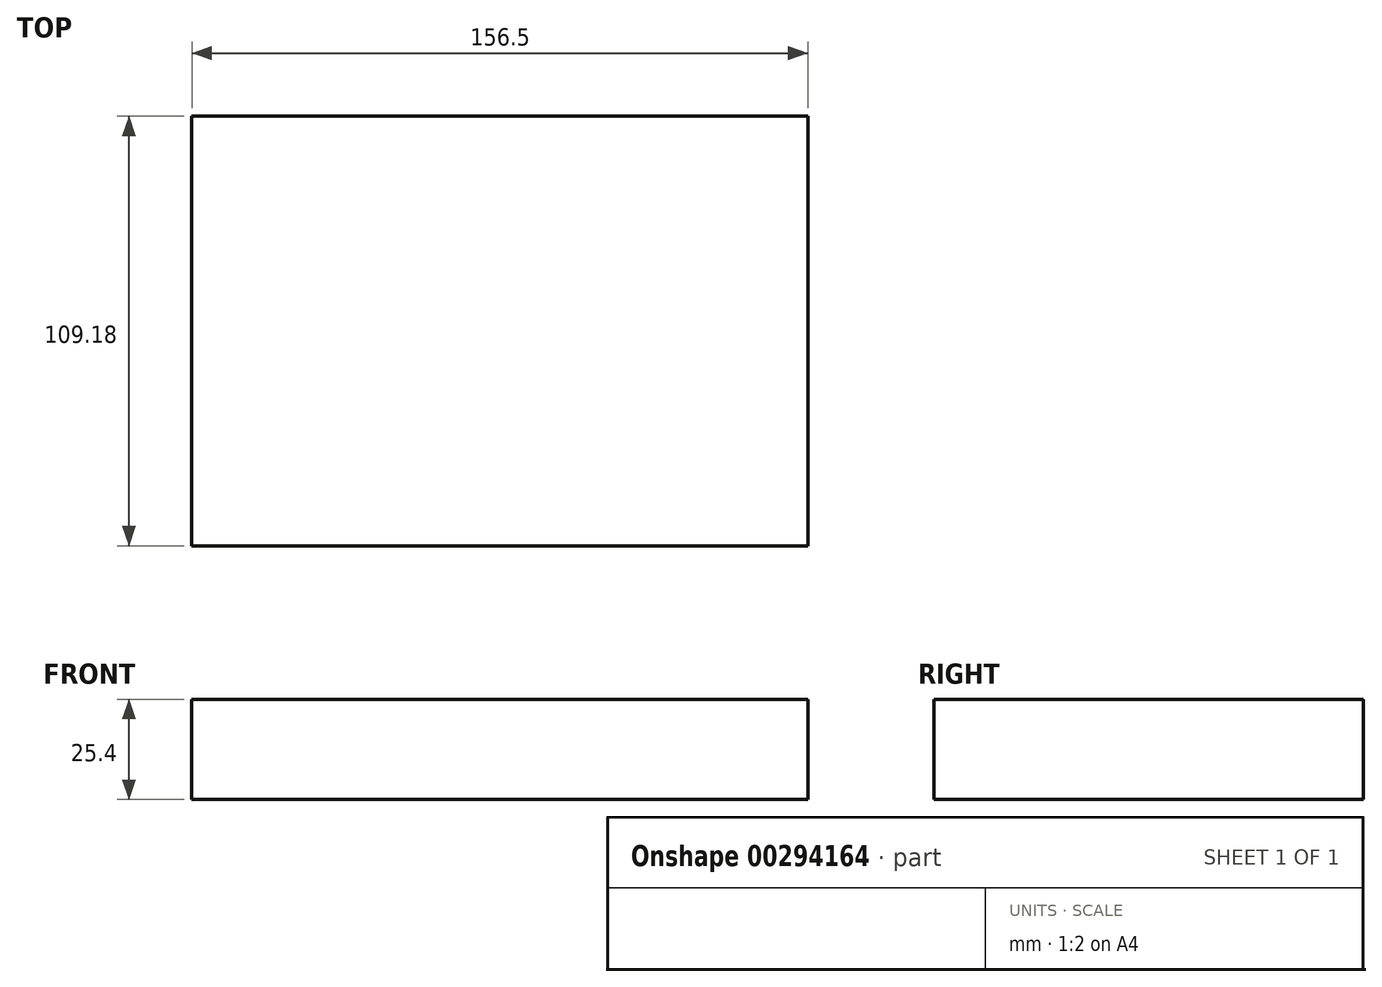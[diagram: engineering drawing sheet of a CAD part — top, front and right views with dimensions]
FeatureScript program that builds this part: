
annotation { "Feature Type Name" : "Feature", "Feature Type Description" : "" }
export const myFeature = defineFeature(function(context is Context, id is Id, definition is map)
    precondition{}
    {
        {
            var Q0;
            Q0=qCreatedBy(makeId("Top.planeOp"),FACE);
            var sketch = newSketch(context, id + "F0", { "sketchPlane" : qUnion([Q0])});
            skLineSegment(sketch, "E0.bottom", {"start": v(-75.96, 32.18) * mm, "end": v(80.54, 32.18) * mm});
            skLineSegment(sketch, "E0.top", {"start": v(-75.96, -77) * mm, "end": v(80.54, -77) * mm});
            skLineSegment(sketch, "E0.left", {"start": v(-75.96, 32.18) * mm, "end": v(-75.96, -77) * mm});
            skLineSegment(sketch, "E0.right", {"start": v(80.54, 32.18) * mm, "end": v(80.54, -77) * mm});
            skSolve(sketch);
        }
        {
            var Q0;
            Q0 = qSketchRegion(id + "F0", true);
            extrude(context, id + "F1", {"entities" : qUnion([Q0]), "depth" : 25.4 * mm});
        }
    });
